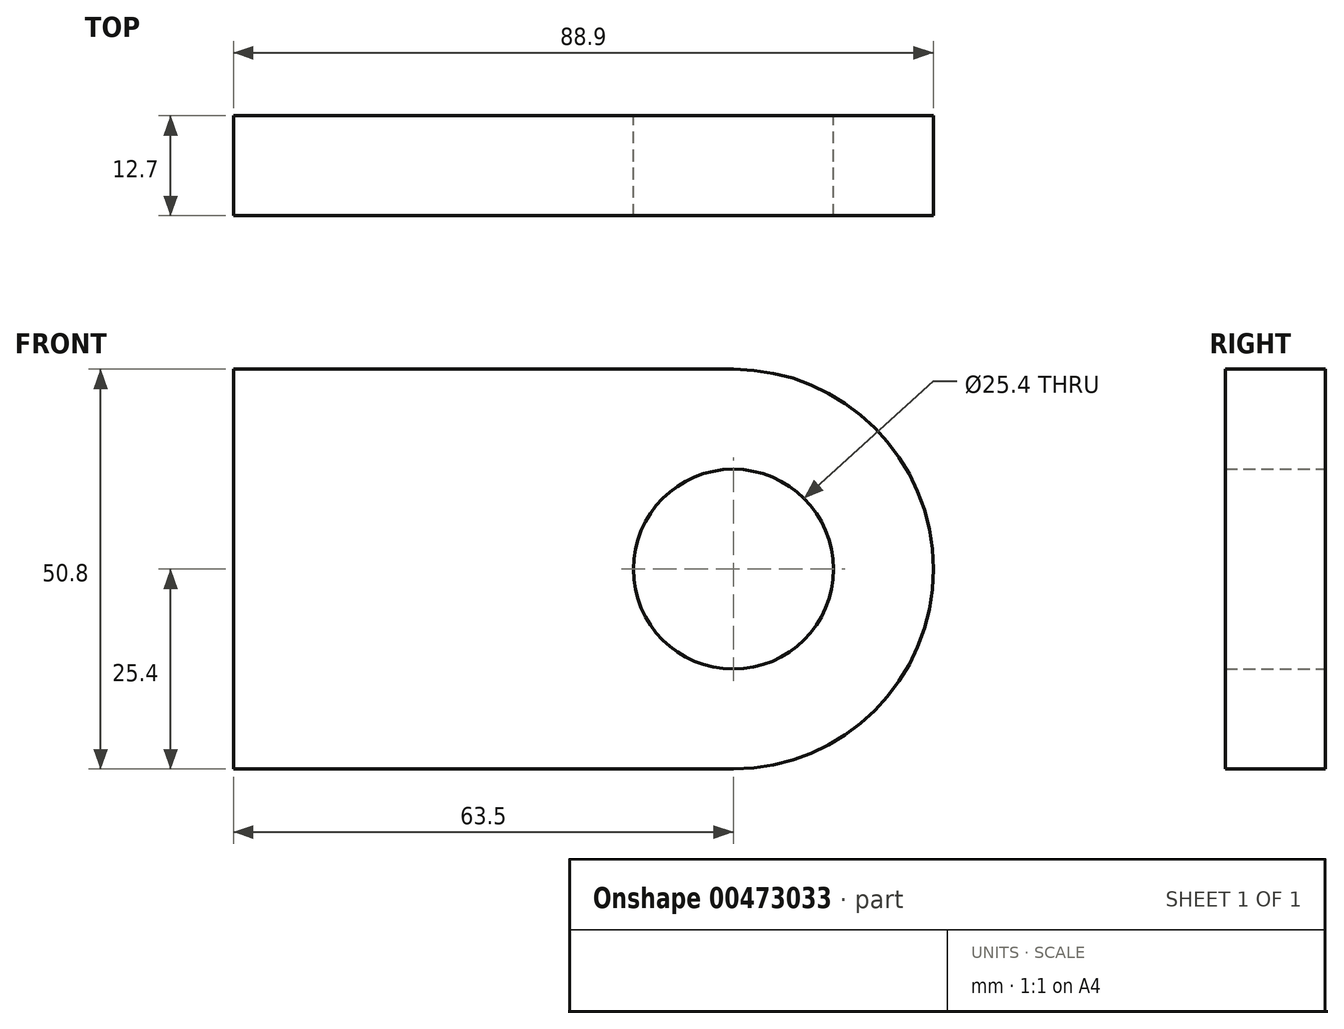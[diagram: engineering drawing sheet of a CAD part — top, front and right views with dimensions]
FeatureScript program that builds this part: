
annotation { "Feature Type Name" : "Feature", "Feature Type Description" : "" }
export const myFeature = defineFeature(function(context is Context, id is Id, definition is map)
    precondition{}
    {
        {
            var Q0;
            Q0=qCreatedBy(makeId("Front.planeOp"),FACE);
            var sketch = newSketch(context, id + "F0", { "sketchPlane" : qUnion([Q0])});
            skLineSegment(sketch, "E0.bottom", {"start": v(19.05, 25.4) * mm, "end": v(-44.45, 25.4) * mm});
            skLineSegment(sketch, "E0.top", {"start": v(19.05, -25.4) * mm, "end": v(-44.45, -25.4) * mm});
            skLineSegment(sketch, "E0.right", {"start": v(-44.45, 25.4) * mm, "end": v(-44.45, -25.4) * mm});
            skPoint(sketch, "E0.middle", {"position": v(0, 0) * mm});
            skPoint(sketch, "E1.endSnap0", {"position": v(44.45, 0) * mm});
            skCircle(sketch, "E2", {"center": v(19.05, 0) * mm, "radius": 12.7 * mm});
            skArc(sketch, "E3", {"start": v(19.05, -25.4) * mm, "mid": v(44.45, 0) * mm, "end": v(19.05, 25.4) * mm});
            skPoint(sketch, "E4.orphan", {"position": v(44.45, 25.4) * mm});
            skPoint(sketch, "E5.orphan", {"position": v(44.45, -25.4) * mm});
            skSolve(sketch);
        }
        {
            var Q0;
            Q0=makeQuery(id+"F0.imprint","IMPRINT",FACE,{"disambiguationData":[TD([[makeQuery(id+"F0.imprint","IMPRINT",EDGE,{"derivedFrom":sQuery(id+"F0.wireOp",EDGE,"E0.bottom")}),1.0]])]});
            extrude(context, id + "F1", {"entities" : qUnion([Q0]), "depth" : 12.7 * mm});
        }
    });
